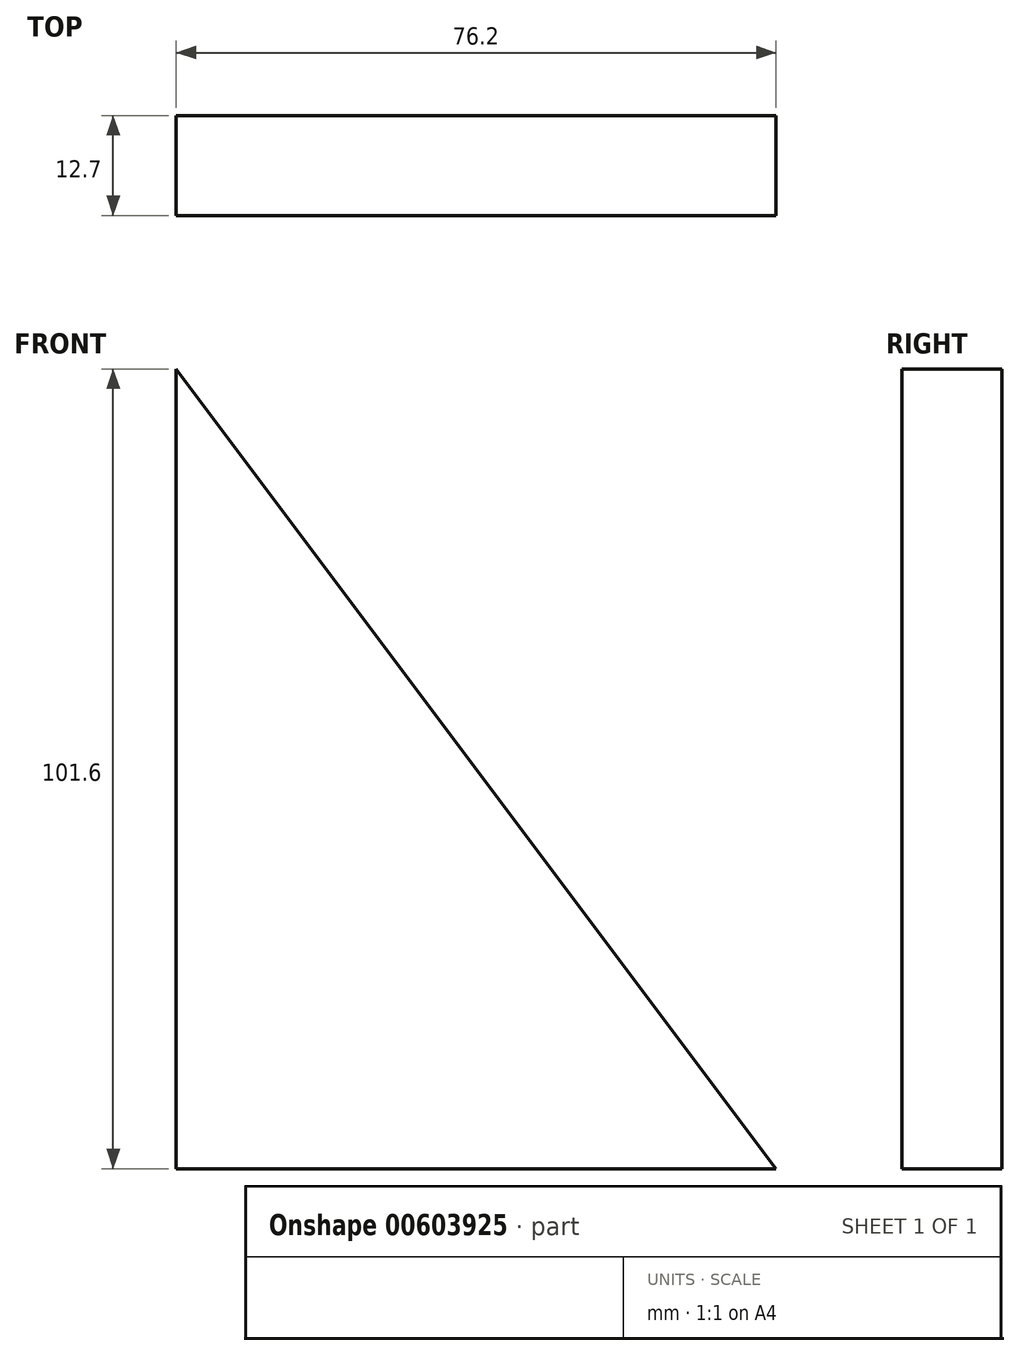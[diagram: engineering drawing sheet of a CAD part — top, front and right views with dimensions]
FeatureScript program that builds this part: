
annotation { "Feature Type Name" : "Feature", "Feature Type Description" : "" }
export const myFeature = defineFeature(function(context is Context, id is Id, definition is map)
    precondition{}
    {
        {
            var Q0;
            Q0=qCreatedBy(makeId("Front.planeOp"),FACE);
            var sketch = newSketch(context, id + "F0", { "sketchPlane" : qUnion([Q0])});
            skLineSegment(sketch, "E0", {"start": v(0, 0) * mm, "end": v(76.2, 0) * mm});
            skLineSegment(sketch, "E1", {"start": v(76.2, 0) * mm, "end": v(0, 101.6) * mm});
            skLineSegment(sketch, "E2", {"start": v(0, 101.6) * mm, "end": v(0, 0) * mm});
            skSolve(sketch);
        }
        {
            var Q0;
            Q0=makeQuery(id+"F0.imprint","IMPRINT",FACE,{"disambiguationData":[TD([[makeQuery(id+"F0.imprint","IMPRINT",EDGE,{"derivedFrom":sQuery(id+"F0.wireOp",EDGE,"E0")}),1.0]])]});
            extrude(context, id + "F1", {"entities" : qUnion([Q0]), "depth" : 12.7 * mm, "offsetDistance" : 25.4 * mm});
        }
    });
